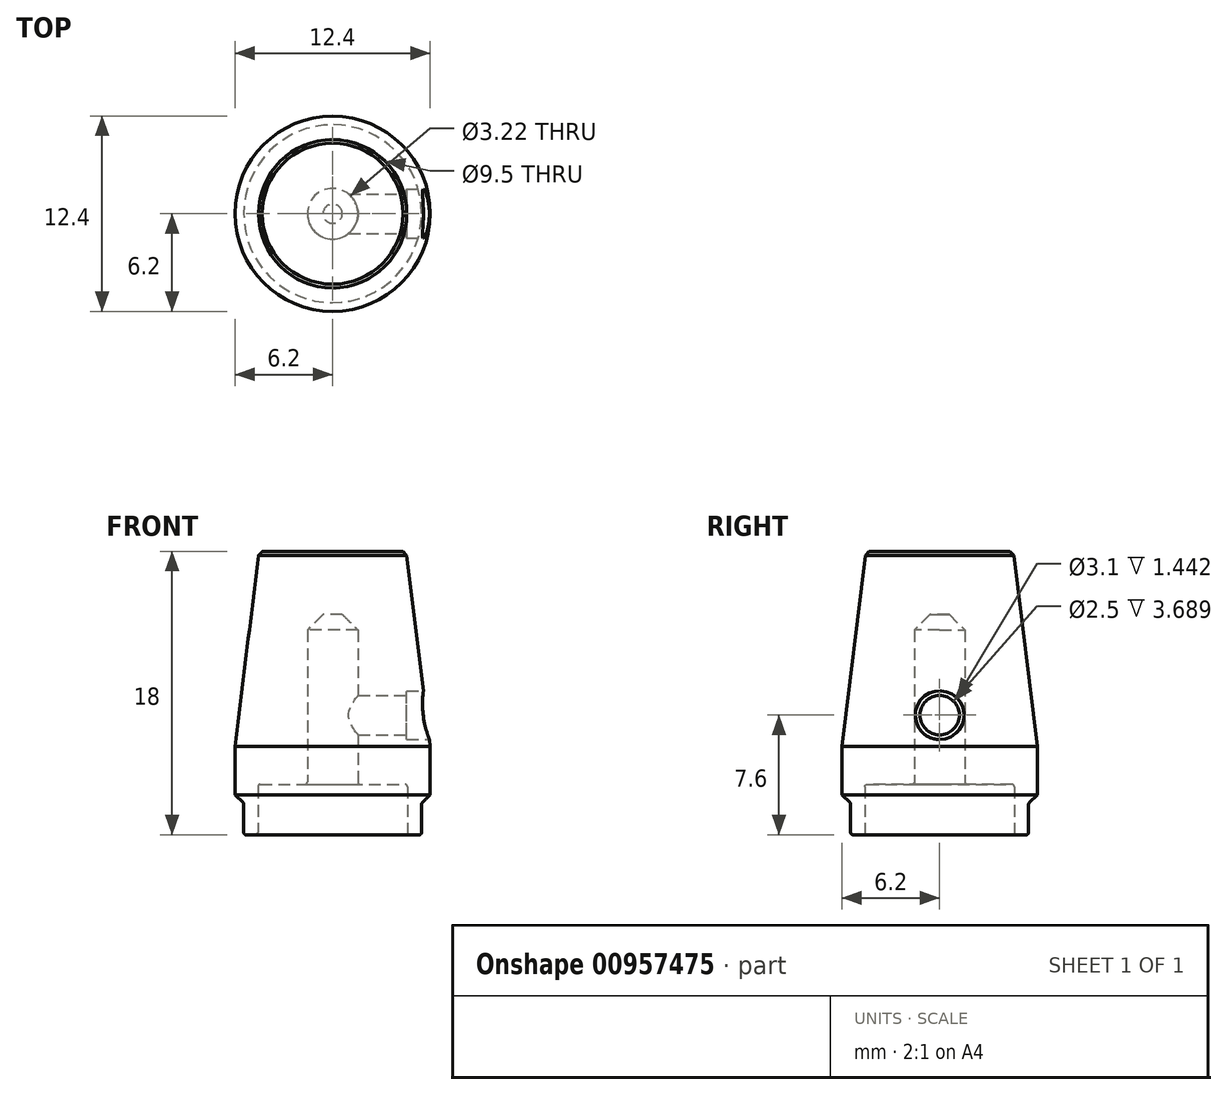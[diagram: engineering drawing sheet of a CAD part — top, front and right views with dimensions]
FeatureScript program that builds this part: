
annotation { "Feature Type Name" : "Feature", "Feature Type Description" : "" }
export const myFeature = defineFeature(function(context is Context, id is Id, definition is map)
    precondition{}
    {
        {
            var Q0;
            Q0=qCreatedBy(makeId("Front.planeOp"),FACE);
            var sketch = newSketch(context, id + "F0", { "sketchPlane" : qUnion([Q0])});
            skLineSegment(sketch, "E0.bottom", {"start": v(4.75, 0) * mm, "end": v(5.65, 0) * mm});
            skLineSegment(sketch, "E0.top", {"start": v(0, 18) * mm, "end": v(4.68, 18) * mm});
            skLineSegment(sketch, "E0.left", {"start": v(0, 3.2) * mm, "end": v(0, 18) * mm, "construction": true});
            skLineSegment(sketch, "E0.right", {"start": v(6.2, 2) * mm, "end": v(6.2, 5.6) * mm});
            skLineSegment(sketch, "E1", {"start": v(1.6, 3.2) * mm, "end": v(4.75, 3.2) * mm});
            skLineSegment(sketch, "E2", {"start": v(4.75, 3.2) * mm, "end": v(4.75, 0) * mm});
            skLineSegment(sketch, "E3", {"start": v(5.65, 0) * mm, "end": v(5.65, 2) * mm});
            skLineSegment(sketch, "E4", {"start": v(5.65, 2) * mm, "end": v(6.2, 2) * mm});
            skLineSegment(sketch, "E5", {"start": v(1.6, 3.2) * mm, "end": v(1.6, 14) * mm});
            skLineSegment(sketch, "E6", {"start": v(1.6, 14) * mm, "end": v(0, 14) * mm});
            skLineSegment(sketch, "E7", {"start": v(0, 18) * mm, "end": v(0, 14) * mm});
            skPoint(sketch, "E8", {"position": v(0, 7.6) * mm});
            skLineSegment(sketch, "E9", {"start": v(4.68, 18) * mm, "end": v(6.2, 5.6) * mm});
            skLineSegment(sketch, "E10", {"start": v(6.2, 5.6) * mm, "end": v(6.2, 20.36) * mm, "construction": true});
            skPoint(sketch, "E11", {"position": v(0, 0) * mm});
            skLineSegment(sketch, "E12", {"start": v(0, 7.6) * mm, "end": v(6.2, 7.6) * mm, "construction": true});
            skPoint(sketch, "E13", {"position": v(6.2, 7.6) * mm});
            skSolve(sketch);
        }
        {
            var Q0;
            Q0=qSketchRegion(id+"F0",true);
            var Q1;
            Q1=sQuery(id+"F0.wireOp",EDGE,"E0.left");
            revolve(context, id + "F1", {"entities" : qUnion([Q0]), "axis" : qUnion([Q1]), "revolveType" : RevolveType.FULL});
        }
        {
            var Q0;
            Q0=makeQuery(id+"F1.opRevolve","SWEPT_EDGE",EDGE,{"disambiguationData":[OSD([sQuery(id+"F0.wireOp",EDGE,"E0.right"),sQuery(id+"F0.wireOp",EDGE,"E4")])]});
            chamfer(context, id + "F2", {"entities" : qUnion([Q0]), "width" : .55 * mm});
        }
        {
            var Q0;
            Q0=makeQuery(id+"F1.opRevolve","SWEPT_EDGE",EDGE,{"disambiguationData":[OSD([sQuery(id+"F0.wireOp",EDGE,"E5"),sQuery(id+"F0.wireOp",EDGE,"E6")])]});
            chamfer(context, id + "F3", {"entities" : qUnion([Q0]), "width" : 1 * mm, "tangentPropagation" : true});
        }
        {
            var Q0;
            Q0=makeQuery(id+"F1.opRevolve","SWEPT_EDGE",EDGE,{"disambiguationData":[OSD([sQuery(id+"F0.wireOp",EDGE,"E0.top"),sQuery(id+"F0.wireOp",EDGE,"E9")])]});
            chamfer(context, id + "F4", {"entities" : qUnion([Q0]), "chamferType" : ChamferType.TWO_OFFSETS, "width1" : .25 * mm, "oppositeDirection" : false, "width2" : .2 * mm, "tangentPropagation" : true});
        }
        {
            var Q0;
            Q0=makeQuery(id+"F1.opRevolve","SWEPT_FACE",FACE,{"disambiguationData":[OSD([sQuery(id+"F0.wireOp",EDGE,"E0.bottom")])]});
            var Q1;
            Q1=makeQuery(id+"F1.opRevolve","SWEPT_EDGE",EDGE,{"disambiguationData":[OSD([sQuery(id+"F0.wireOp",EDGE,"E1"),sQuery(id+"F0.wireOp",EDGE,"E2")])]});
            var Q2;
            Q2=makeQuery(id+"F1.opRevolve","SWEPT_EDGE",EDGE,{"disambiguationData":[OSD([sQuery(id+"F0.wireOp",EDGE,"E1"),sQuery(id+"F0.wireOp",EDGE,"E5")])]});
            var Q3;
            Q3=makeQuery(id+"F2.opChamfer","BLEND_EDGE",EDGE,{"blendedFrom":[makeQuery(id+"F1.opRevolve","SWEPT_EDGE",EDGE,{"disambiguationData":[OSD([sQuery(id+"F0.wireOp",EDGE,"E0.right"),sQuery(id+"F0.wireOp",EDGE,"E4")])]}),makeQuery(id+"F1.opRevolve","SWEPT_FACE",FACE,{"disambiguationData":[OSD([sQuery(id+"F0.wireOp",EDGE,"E3")])]})],"blendedInto":[makeQuery(id+"F1.opRevolve","SWEPT_FACE",FACE,{"disambiguationData":[OSD([sQuery(id+"F0.wireOp",EDGE,"E3")])]})]});
            fillet(context, id + "F5", {"entities" : qUnion([Q0, Q1, Q2, Q3]), "radius" : 0.15 * mm, "tangentPropagation" : true, "allowEdgeOverflow" : false});
        }
        {
            var Q0;
            Q0=sQuery(id+"F0.wireOp",EDGE,"E0.right");
            cPlane(context, id + "F6", {"entities" : qUnion([Q0]), "cplaneType" : CPlaneType.LINE_ANGLE, "offset" : 25 * mm, "angle" : 0 * degree, "width" : 150 * mm, "height" : 150 * mm});
        }
        {
            var Q0;
            Q0=qCreatedBy(id+"F6.planeOp",FACE);
            var sketch = newSketch(context, id + "F7", { "sketchPlane" : qUnion([Q0])});
            skPoint(sketch, "E14.0", {"position": v(0, 7.6) * mm});
            skSolve(sketch);
        }
        {
            var Q0;
            Q0=sQuery(id+"F7.wireOp",VERTEX,"E14.0");
            var Q1;
            Q1=makeQuery(id+"F1.opRevolve","SWEPT_BODY",BODY,{"disambiguationData":[OSD([sQuery(id+"F0.wireOp",EDGE,"E0.bottom"),sQuery(id+"F0.wireOp",EDGE,"E0.top"),sQuery(id+"F0.wireOp",EDGE,"E0.right"),sQuery(id+"F0.wireOp",EDGE,"E1"),sQuery(id+"F0.wireOp",EDGE,"E2"),sQuery(id+"F0.wireOp",EDGE,"E3"),sQuery(id+"F0.wireOp",EDGE,"E4"),sQuery(id+"F0.wireOp",EDGE,"E5"),sQuery(id+"F0.wireOp",EDGE,"E6"),sQuery(id+"F0.wireOp",EDGE,"E7"),sQuery(id+"F0.wireOp",EDGE,"E9")])]});
            hole(context, id + "F8", {"style" : HoleStyle.C_BORE, "endStyle" : HoleEndStyle.BLIND, "holeDiameter" : 2.5 * mm, "cBoreDiameter" : 3.1 * mm, "cBoreDepth" : 1 * mm, "holeDepth" : 5 * mm, "isTappedThrough" : true, "tappedDepth" : 12 * mm, "tapClearance" : 3, "locations" : qUnion([Q0]), "scope" : qUnion([Q1])});
        }
    });
